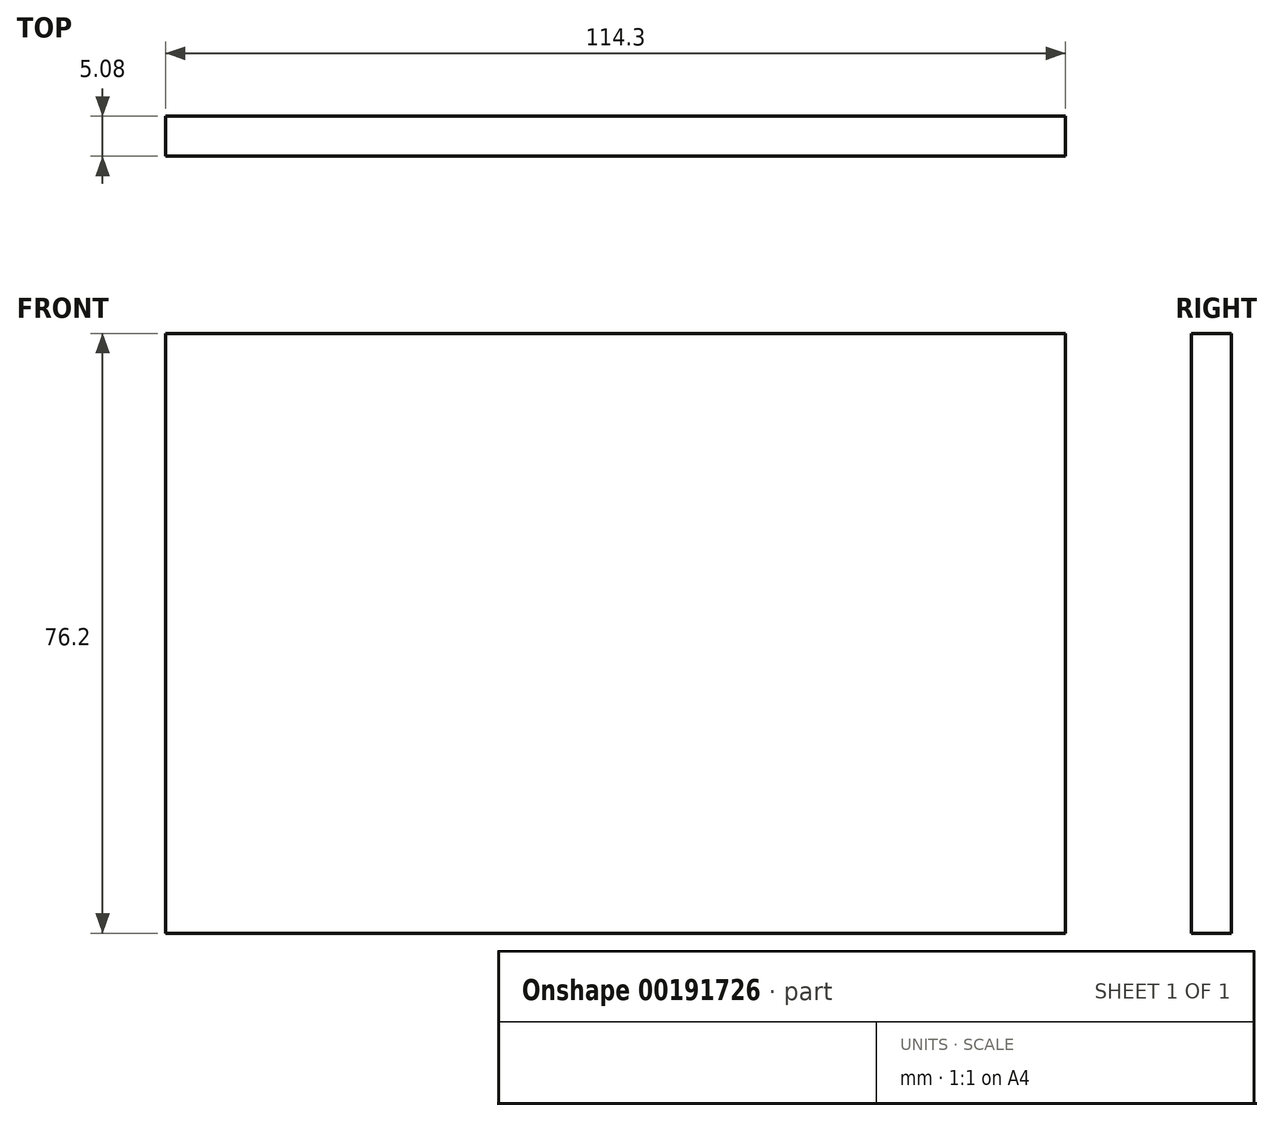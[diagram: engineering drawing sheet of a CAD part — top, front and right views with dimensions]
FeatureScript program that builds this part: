
annotation { "Feature Type Name" : "Feature", "Feature Type Description" : "" }
export const myFeature = defineFeature(function(context is Context, id is Id, definition is map)
    precondition{}
    {
        {
            var Q0;
            Q0=qCreatedBy(makeId("Front.planeOp"),FACE);
            var sketch = newSketch(context, id + "F0", { "sketchPlane" : qUnion([Q0])});
            skLineSegment(sketch, "E0.bottom", {"start": v(-79.26, 73.88) * mm, "end": v(35.04, 73.88) * mm});
            skLineSegment(sketch, "E0.top", {"start": v(-79.26, -2.32) * mm, "end": v(35.04, -2.32) * mm});
            skLineSegment(sketch, "E0.left", {"start": v(-79.26, 73.88) * mm, "end": v(-79.26, -2.32) * mm});
            skLineSegment(sketch, "E0.right", {"start": v(35.04, 73.88) * mm, "end": v(35.04, -2.32) * mm});
            skSolve(sketch);
        }
        {
            var Q0;
            Q0=makeQuery(id+"F0.imprint","IMPRINT",FACE,{"disambiguationData":[TD([[makeQuery(id+"F0.imprint","IMPRINT",EDGE,{"derivedFrom":sQuery(id+"F0.wireOp",EDGE,"E0.bottom")}),-1.0]])]});
            extrude(context, id + "F1", {"entities" : qUnion([Q0]), "depth" : 5.08 * mm});
        }
    });
